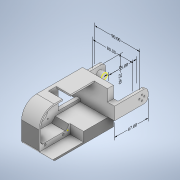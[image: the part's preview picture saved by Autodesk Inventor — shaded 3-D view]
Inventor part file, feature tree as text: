
AUTODESK INVENTOR PART (.ipt)
format: ipt  version: 2022 (Build 260153000, 153)  size: 1,464,320 bytes
history: native  units: mm
features: sketch x35, extrude x33, other x9, fillet x3, plane x1
ambient origin geometry x8: Origin, YZ Plane, XZ Plane, XY Plane, X Axis, Y Axis, Z Axis, Center Point
bodies: Solid1 (feature_tree)
feature tree (81):
  other  "Assembly2.iam"
  other  "96Gears_Stage_1_modified.ipt:1"
  other  "96Gears_Stage_2_modified.ipt:1"
  other  "Annotations"
  extrude  "Extrusion3"  Depth=10.0mm
  extrude  "Extrusion5"  Depth=18.0mm TaperAngle=0.0deg
  extrude  "Extrusion6"  Depth=6.0mm TaperAngle=0.0deg
  extrude  "Extrusion7"  Depth=10.0mm TaperAngle=0.0deg
  extrude  "Extrusion8"  Depth=4.1mm
  extrude  "Extrusion9"  Depth=7.0mm
  extrude  "Extrusion10"  Depth=50.0mm TaperAngle=0.0deg
  extrude  "Extrusion11"  Depth=50.0mm TaperAngle=0.0deg
  extrude  "Extrusion12"  Depth=3.0mm TaperAngle=0.0deg
  extrude  "Extrusion13"  Depth=3.0mm TaperAngle=0.0deg
  extrude  "Extrusion14"  Depth=9.0mm TaperAngle=0.0deg
  extrude  "Extrusion15"  Depth=9.0mm TaperAngle=0.0deg
  extrude  "Extrusion16"  Depth=30.0mm
  fillet  "Fillet1"  Radius=5.0mm
  extrude  "Extrusion17"  Depth=10.0mm TaperAngle=0.0deg
  extrude  "Extrusion18"  Depth=10.0mm TaperAngle=0.0deg
  extrude  "Extrusion19"  Depth=13.0mm TaperAngle=0.0deg
  extrude  "Extrusion20"  Depth=13.0mm TaperAngle=0.0deg
  extrude  "Extrusion21"  Depth=24.0mm
  extrude  "Extrusion22"  Depth=5.0mm
  extrude  "Extrusion23"  Depth=55.0mm TaperAngle=0.0deg
  extrude  "Extrusion24"  Depth=55.0mm TaperAngle=0.0deg
  extrude  "Extrusion25"  Depth=10.0mm
  fillet  "Fillet2"  Radius=5.0mm
  extrude  "Extrusion26"  Depth=8.0mm TaperAngle=0.0deg
  fillet  "Fillet3"  Radius=12.0mm
  extrude  "Extrusion27"  Depth=10.0mm TaperAngle=0.0deg
  extrude  "Extrusion31"  Depth=16.0mm
  extrude  "Extrusion32"  Depth=10.0mm TaperAngle=0.0deg
  extrude  "Extrusion33"  Depth=10.0mm TaperAngle=0.0deg
  extrude  "Extrusion34"  Depth=10.0mm TaperAngle=0.0deg
  sketch  "Sketch37"  dims[d173=11.5mm]
  plane  "Work Plane3"
  extrude  "Extrusion35"  TaperAngle=0.0deg  [1 undecoded]
  extrude  "Extrusion36"  Depth=0.5mm
  extrude  "Extrusion37"  [1 undecoded]
  extrude  "Extrusion38"  [1 undecoded]
  extrude  "Extrusion39"  [1 undecoded]
  sketch  "Sketch5"  dims[d7=6.0mm d8=18.0mm d9=0.0mm]
  sketch  "Sketch4"  dims[d0=10.0mm d6=3.0mm]
  sketch  "Sketch7"  dims[d17=32.25mm d18=6.0mm d19=0.0mm]
  sketch  "Sketch8"  dims[d20=10.0mm d21=10.0mm d22=0.0mm]
  sketch  "Sketch9"  dims[d24=4.1mm d25=4.1mm]
  sketch  "Sketch10"  dims[d26=10.0mm d27=0.0mm d28=7.0mm]
  sketch  "Sketch11"  dims[d29=0.0mm d30=0.0mm d31=50.0mm d32=0.0mm]
  sketch  "Sketch12"  dims[d33=3.0mm d34=50.0mm d35=0.0mm]
  sketch  "Sketch13"  dims[d38=3.0mm d39=3.0mm d40=0.0mm]
  sketch  "Sketch14"  dims[d41=23.0mm d42=3.0mm d43=0.0mm]
  sketch  "Sketch15"  dims[d44=3.0mm d45=0.0mm d46=9.0mm d47=0.0mm]
  sketch  "Sketch16"  dims[d49=33.25mm d50=9.0mm d51=0.0mm]
  sketch  "Sketch17"  dims[d52=2.0mm d53=0.0mm d54=30.0mm d55=5.0mm]
  sketch  "Sketch18"  dims[d57=5.0mm d58=10.0mm d59=0.0mm]
  sketch  "Sketch19"  dims[d60=3.0mm d61=10.0mm d62=0.0mm]
  sketch  "Sketch20"  dims[d63=2.0mm d64=0.0mm d65=13.0mm d66=0.0mm]
  sketch  "Sketch21"  dims[d67=32.25mm d68=13.0mm d69=0.0mm]
  sketch  "Sketch22"  dims[d76=14.0mm d77=24.0mm]
  sketch  "Sketch23"  dims[d78=12.0mm d79=0.0mm d80=5.0mm]
  sketch  "Sketch24"  dims[d81=5.0mm d82=55.0mm d83=0.0mm]
  sketch  "Sketch25"  dims[d92=40.0mm d94=360.0deg d96=55.0mm d97=0.0mm]
  sketch  "Sketch26"  dims[d101=10.0mm d102=0.0mm d118=5.75mm d119=5.0mm d120=0.0mm]
  sketch  "Sketch27"  dims[d121=8.0mm d125=8.0mm d126=0.0mm d144=12.0mm d145=0.0mm]
  sketch  "Sketch28"  dims[d146=10.0mm d147=0.0mm d148=10.0mm d149=0.0mm]
  sketch  "Sketch29"  dims[d150=8.0mm d151=16.0mm]
  sketch  "Sketch33"  dims[d152=10.0mm d153=0.0mm d156=4.2mm d157=0.0mm]
  sketch  "Sketch34"  dims[d158=10.0mm d159=0.0mm d160=10.0mm d161=0.0mm]
  sketch  "Sketch35"  dims[d163=30.75mm d164=10.0mm d165=0.0mm]
  sketch  "Sketch36"  dims[d170=2.5mm d171=0.0mm d172=0.0mm]
  sketch  "Sketch38"  dims[d103=2.161817mm d104=5.384355mm d105=80.0mm d106=6.851437mm d107=7.526531mm d108=90.0mm d109=2.261432mm d110=4.924128mm d111=55.0mm d112=3.454791mm d113=3.105941mm d114=67.0mm d115=9.287367mm d116=9.070993mm d117=25.4mm d154=0.5mm]
  sketch  "Sketch39"  dims[d155=0.872665mm]
  sketch  "Sketch40"
  sketch  "Sketch42"
  sketch  "Sketch43"
  other  "Linear Dimension 1"
  other  "Linear Dimension 2"
  other  "Linear Dimension 3"
  other  "Linear Dimension 4"
  other  "Linear Dimension 5"
note: 4 required parameter values undecoded (feature->parameter linkage not recoverable at this tier; creation-order binding heuristic only, values carry confidence <= 0.55)
